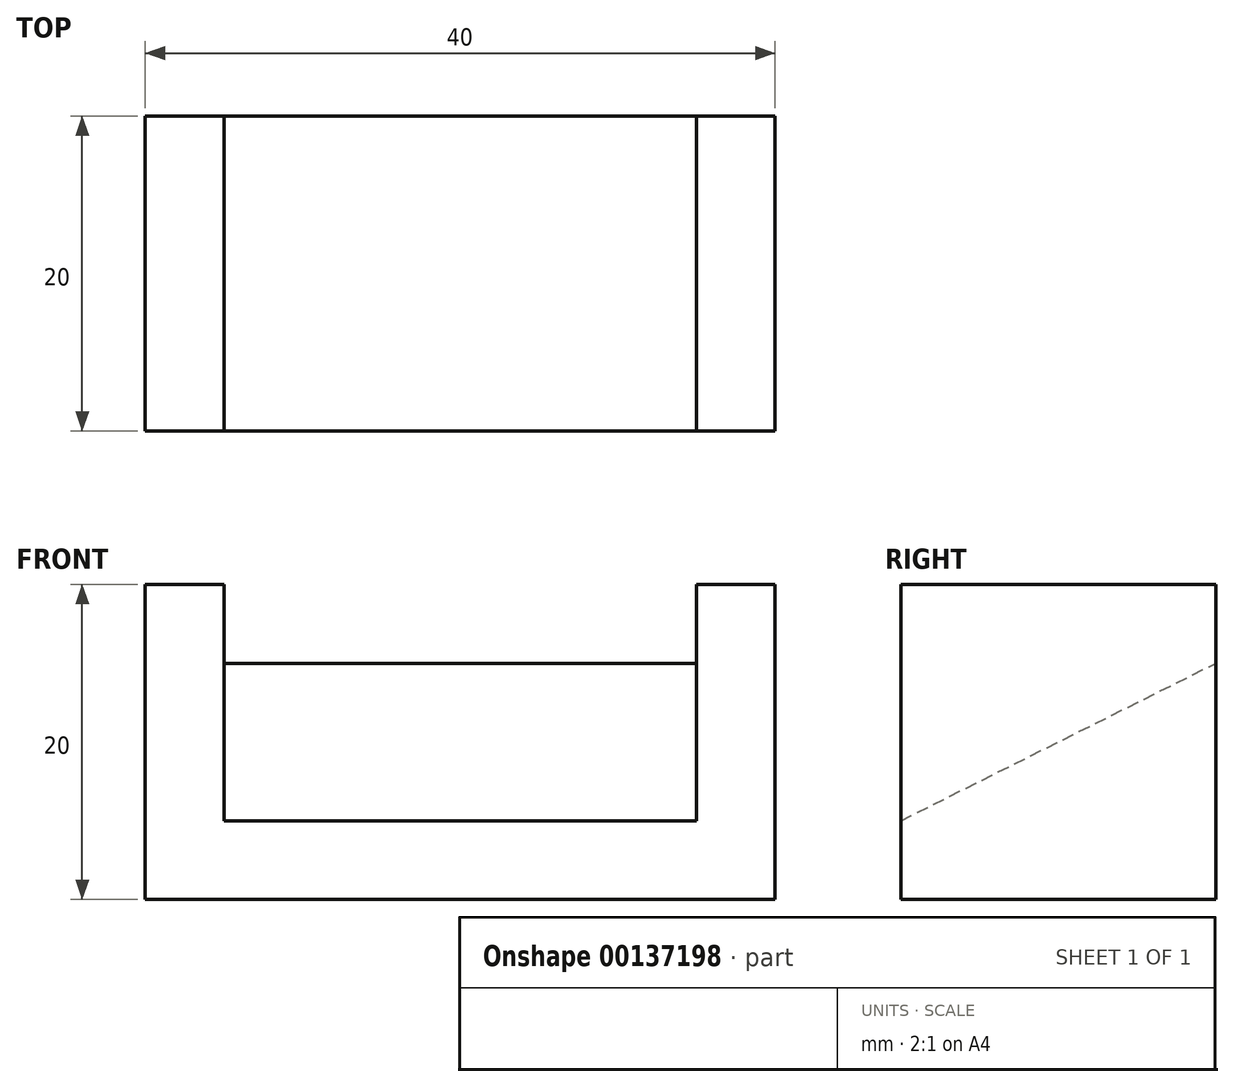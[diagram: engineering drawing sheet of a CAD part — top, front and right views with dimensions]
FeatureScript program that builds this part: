
annotation { "Feature Type Name" : "Feature", "Feature Type Description" : "" }
export const myFeature = defineFeature(function(context is Context, id is Id, definition is map)
    precondition{}
    {
        {
            var Q0;
            Q0=qCreatedBy(makeId("Right.planeOp"),FACE);
            var sketch = newSketch(context, id + "F0", { "sketchPlane" : qUnion([Q0])});
            skLineSegment(sketch, "E0", {"start": v(0, 0) * mm, "end": v(0, 5) * mm});
            skLineSegment(sketch, "E1", {"start": v(0, 5) * mm, "end": v(20, 15) * mm});
            skLineSegment(sketch, "E2", {"start": v(20, 15) * mm, "end": v(20, 0) * mm});
            skLineSegment(sketch, "E3", {"start": v(20, 0) * mm, "end": v(0, 0) * mm});
            skSolve(sketch);
        }
        {
            var Q0;
            Q0 = qSketchRegion(id + "F0", true);
            extrude(context, id + "F1", {"entities" : qUnion([Q0]), "depth" : 30 * mm});
        }
        {
            var Q0;
            Q0=qCreatedBy(makeId("Front.planeOp"),FACE);
            var sketch = newSketch(context, id + "F2", { "sketchPlane" : qUnion([Q0])});
            skLineSegment(sketch, "E4", {"start": v(0, 0) * mm, "end": v(0, 20) * mm});
            skLineSegment(sketch, "E5", {"start": v(0, 20) * mm, "end": v(-5, 20) * mm});
            skLineSegment(sketch, "E6", {"start": v(-5, 20) * mm, "end": v(-5, 0) * mm});
            skLineSegment(sketch, "E7", {"start": v(-5, 0) * mm, "end": v(0, 0) * mm});
            skLineSegment(sketch, "E8.0", {"start": v(30, 0) * mm, "end": v(30, 5) * mm});
            skLineSegment(sketch, "E9.0", {"start": v(30, 5) * mm, "end": v(30, 15) * mm});
            skLineSegment(sketch, "E10", {"start": v(30, 0) * mm, "end": v(30, 20) * mm});
            skPoint(sketch, "E10.endSnap0", {"position": v(30, 10) * mm});
            skLineSegment(sketch, "E11", {"start": v(30, 20) * mm, "end": v(35, 20) * mm});
            skLineSegment(sketch, "E12", {"start": v(35, 20) * mm, "end": v(35, 0) * mm});
            skLineSegment(sketch, "E13", {"start": v(35, 0) * mm, "end": v(30, 0) * mm});
            skSolve(sketch);
        }
        {
            var Q0;
            Q0 = qSketchRegion(id + "F2", true);
            extrude(context, id + "F3", {"entities" : qUnion([Q0]), "operationType" : NewBodyOperationType.ADD, "oppositeDirection" : true, "depth" : 20 * mm});
        }
    });
